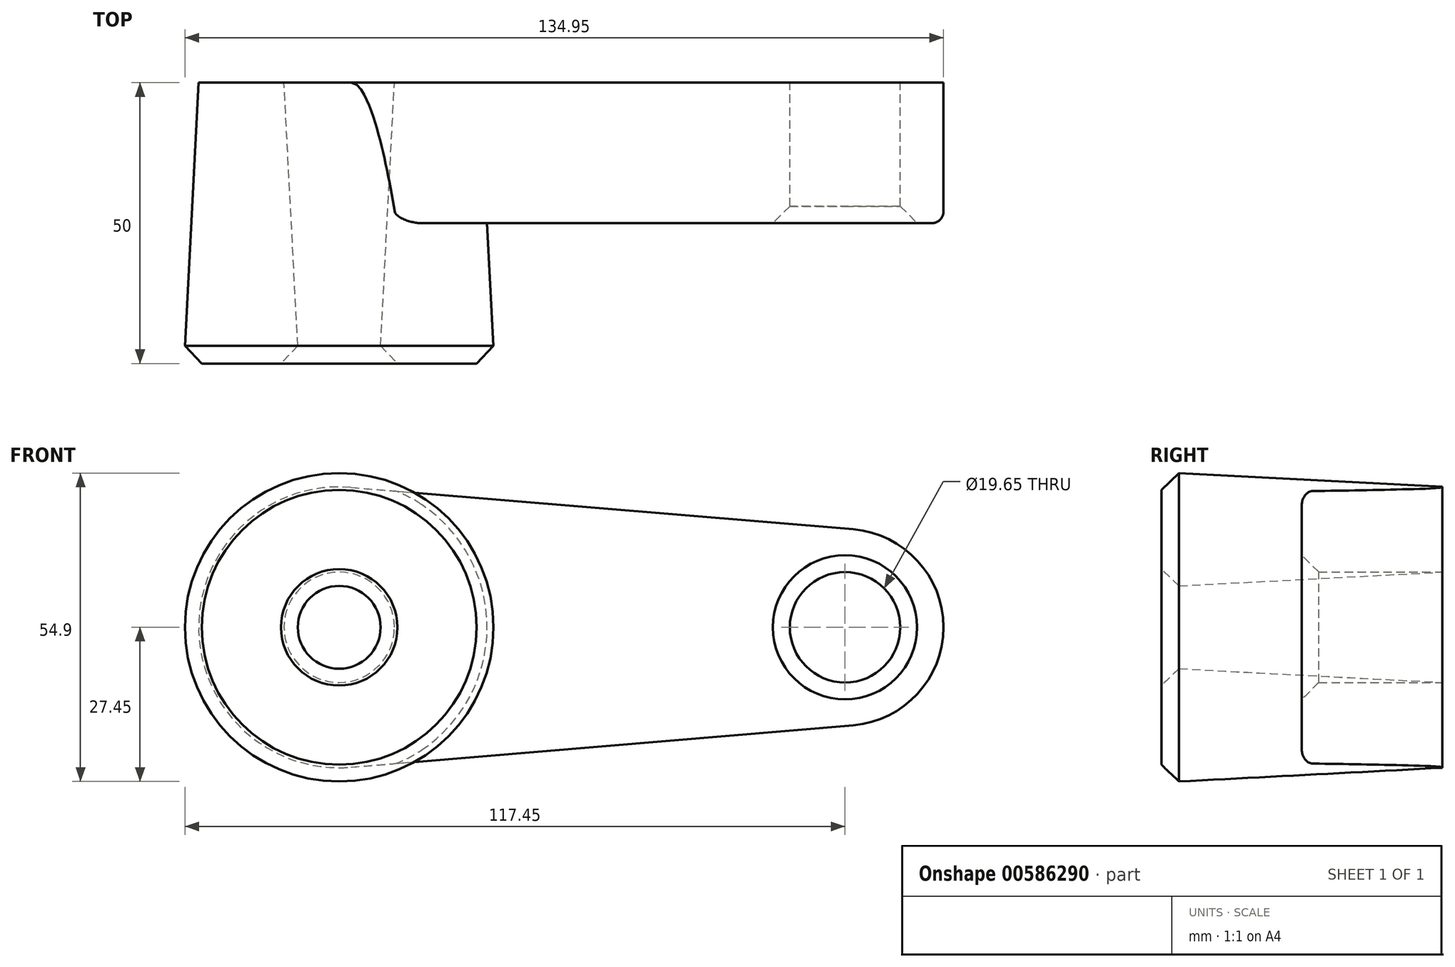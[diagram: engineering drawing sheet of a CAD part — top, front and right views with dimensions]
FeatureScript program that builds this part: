
annotation { "Feature Type Name" : "Feature", "Feature Type Description" : "" }
export const myFeature = defineFeature(function(context is Context, id is Id, definition is map)
    precondition{}
    {
        {
            var Q0;
            Q0=qCreatedBy(makeId("Front.planeOp"),FACE);
            var sketch = newSketch(context, id + "F0", { "sketchPlane" : qUnion([Q0])});
            skCircle(sketch, "E0", {"center": v(0, 0) * mm, "radius": 25 * mm});
            skCircle(sketch, "E1", {"center": v(90, 0) * mm, "radius": 17.5 * mm});
            skCircle(sketch, "E2", {"center": v(0, 0) * mm, "radius": 9.82 * mm});
            skCircle(sketch, "E3", {"center": v(90, 0) * mm, "radius": 9.82 * mm});
            skLineSegment(sketch, "E4", {"start": v(2.08, 24.91) * mm, "end": v(91.46, 17.44) * mm});
            skLineSegment(sketch, "E5", {"start": v(2.08, -24.91) * mm, "end": v(91.46, -17.44) * mm});
            skSolve(sketch);
        }
        {
            var Q0;
            {var subQ0=sQuery(id+"F0.wireOp",EDGE,"E4");Q0=makeQuery(id+"F0.imprint","IMPRINT",FACE,{"disambiguationData":[TD([[makeQuery(id+"F0.imprint","IMPRINT",EDGE,{"derivedFrom":subQ0}),-1.0]])]});}
            var Q1;
            Q1=makeQuery(id+"F0.imprint","IMPRINT",FACE,{"disambiguationData":[TD([[makeQuery(id+"F0.imprint","IMPRINT",EDGE,{"derivedFrom":sQuery(id+"F0.wireOp",EDGE,"E2")}),-1.0]])]});
            var Q2;
            Q2 = qSketchRegion(id + "F0", true);
            var Q3;
            Q3=makeQuery(id+"F0.imprint","IMPRINT",FACE,{"disambiguationData":[TD([[makeQuery(id+"F0.imprint","IMPRINT",EDGE,{"derivedFrom":sQuery(id+"F0.wireOp",EDGE,"E3")}),-1.0]])]});
            extrude(context, id + "F1", {"entities" : qUnion([Q0, Q1, Q2, Q3]), "depth" : 25 * mm, "offsetDistance" : 25 * mm});
        }
        {
            var Q0;
            Q0=makeQuery(id+"F0.imprint","IMPRINT",FACE,{"disambiguationData":[TD([[makeQuery(id+"F0.imprint","IMPRINT",EDGE,{"derivedFrom":sQuery(id+"F0.wireOp",EDGE,"E2")}),-1.0]])]});
            extrude(context, id + "F2", {"entities" : qUnion([Q0]), "operationType" : NewBodyOperationType.ADD, "depth" : 50 * mm, "offsetDistance" : 25 * mm, "hasDraft" : true, "draftAngle" : 3 * degree});
        }
        {
            var Q0;
            Q0=makeQuery(id+"F1.opExtrude","CAP_EDGE",EDGE,{"disambiguationData":[OSD([sQuery(id+"F0.wireOp",EDGE,"E3")])],"isStart":false});
            var Q1;
            Q1=makeQuery(id+"F2.opExtrude","CAP_EDGE",EDGE,{"disambiguationData":[OSD([sQuery(id+"F0.wireOp",EDGE,"E2")])],"isStart":false});
            var Q2;
            Q2=makeQuery(id+"F2.opExtrude","CAP_EDGE",EDGE,{"disambiguationData":[OSD([sQuery(id+"F0.wireOp",EDGE,"E0")])],"isStart":false});
            chamfer(context, id + "F3", {"entities" : qUnion([Q0, Q1, Q2]), "width" : 3 * mm, "tangentPropagation" : true});
        }
        {
            var Q0;
            Q0=makeQuery(id+"F1.opExtrude","CAP_EDGE",EDGE,{"disambiguationData":[OSD([sQuery(id+"F0.wireOp",EDGE,"E5")])],"isStart":false});
            fillet(context, id + "F4", {"entities" : qUnion([Q0]), "radius" : 2 * mm, "tangentPropagation" : true, "allowEdgeOverflow" : false});
        }
    });
